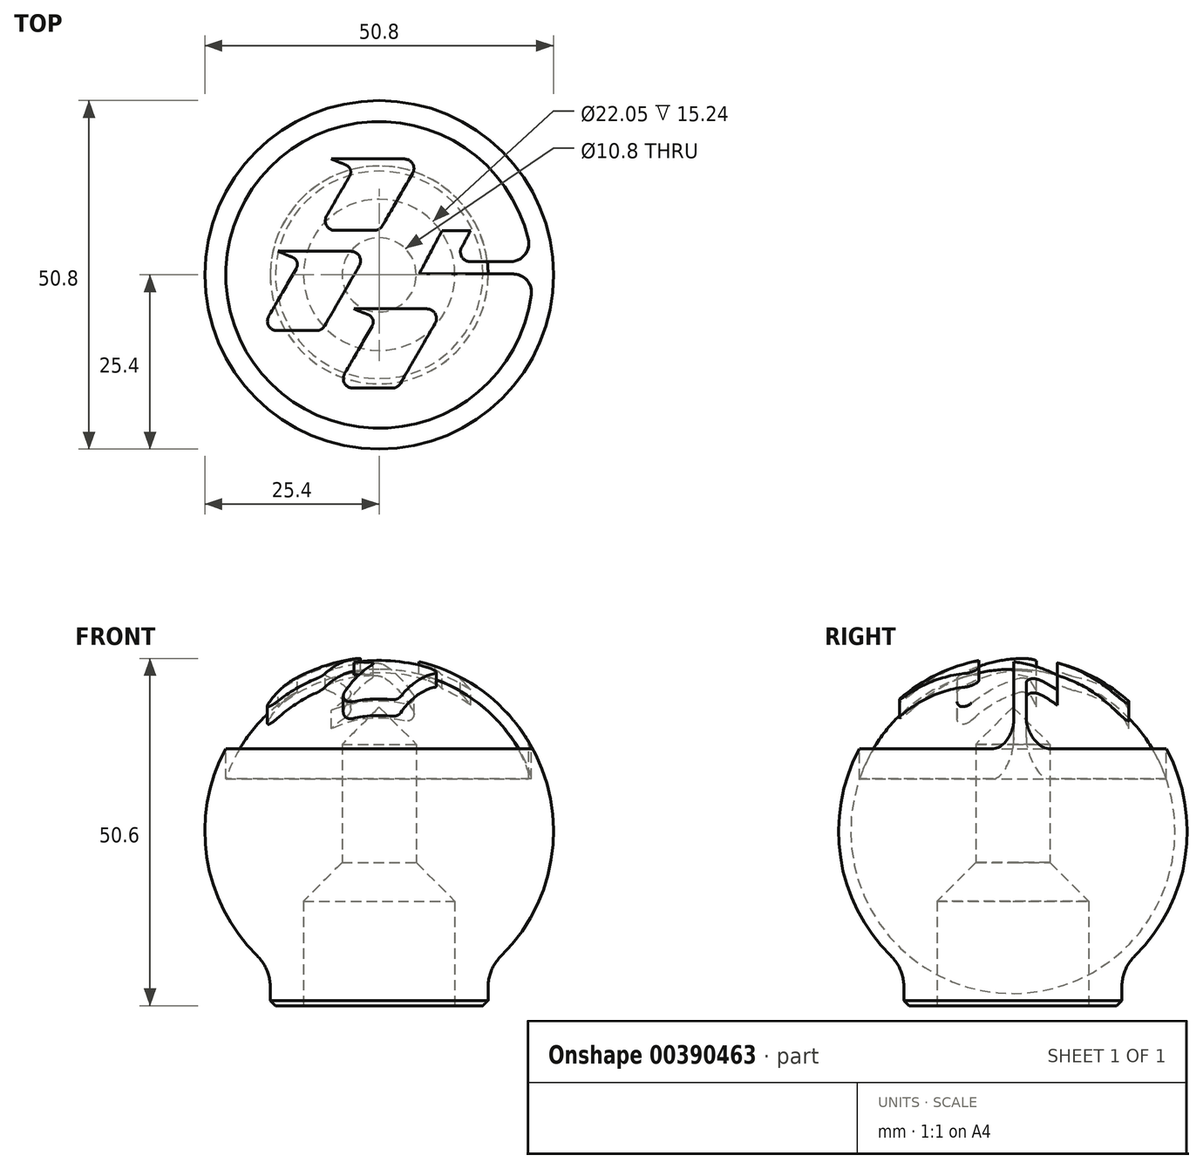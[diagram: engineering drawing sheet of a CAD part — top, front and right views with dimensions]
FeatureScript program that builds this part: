
annotation { "Feature Type Name" : "Feature", "Feature Type Description" : "" }
export const myFeature = defineFeature(function(context is Context, id is Id, definition is map)
    precondition{}
    {
        {
            var Q0;
            Q0=qCreatedBy(makeId("Top.planeOp"),FACE);
            cPlane(context, id + "F0", {"entities" : qUnion([Q0]), "cplaneType" : CPlaneType.OFFSET, "offset" : 50.8 * mm, "width" : 152.4 * mm, "height" : 152.4 * mm});
        }
        {
            var Q0;
            Q0=qCreatedBy(makeId("Front.planeOp"),FACE);
            var sketch = newSketch(context, id + "F1", { "sketchPlane" : qUnion([Q0])});
            skLineSegment(sketch, "E0", {"start": v(0, 0) * mm, "end": v(0, 50.8) * mm});
            skArc(sketch, "E1", {"start": v(17.78, 7.26) * mm, "mid": v(23.51, 35) * mm, "end": v(0, 50.8) * mm});
            skArc(sketch, "E2", {"start": v(17.78, 7.26) * mm, "mid": v(16.37, 5.19) * mm, "end": v(15.88, 2.73) * mm});
            skLineSegment(sketch, "E3", {"start": v(15.88, 2.73) * mm, "end": v(15.88, 0) * mm});
            skLineSegment(sketch, "E4", {"start": v(15.88, 0) * mm, "end": v(0, 0) * mm});
            skSolve(sketch);
        }
        {
            var Q0;
            Q0=makeQuery(id+"F1.imprint","IMPRINT",FACE,{"disambiguationData":[TD([[makeQuery(id+"F1.imprint","IMPRINT",EDGE,{"derivedFrom":sQuery(id+"F1.wireOp",EDGE,"E0")}),-1.0]])]});
            var Q1;
            Q1=sQuery(id+"F1.wireOp",EDGE,"E0");
            revolve(context, id + "F2", {"entities" : qUnion([Q0]), "axis" : qUnion([Q1]), "revolveType" : RevolveType.FULL});
        }
        {
            var Q0;
            Q0=makeQuery(id+"F2.opRevolve","SWEPT_FACE",FACE,{"disambiguationData":[OSD([sQuery(id+"F1.wireOp",EDGE,"E4")])]});
            var sketch = newSketch(context, id + "F3", { "sketchPlane" : qUnion([Q0])});
            skCircle(sketch, "E5", {"center": v(0, 0) * mm, "radius": 5.4 * mm});
            skSolve(sketch);
        }
        {
            var Q0;
            Q0=makeQuery(id+"F2.opRevolve","SWEPT_FACE",FACE,{"disambiguationData":[OSD([sQuery(id+"F1.wireOp",EDGE,"E4")])]});
            var sketch = newSketch(context, id + "F4", { "sketchPlane" : qUnion([Q0])});
            skCircle(sketch, "E6", {"center": v(0, 0) * mm, "radius": 11.02 * mm});
            skSolve(sketch);
        }
        {
            var Q0;
            Q0=qCreatedBy(makeId("Top.planeOp"),FACE);
            var sketch = newSketch(context, id + "F5", { "sketchPlane" : qUnion([Q0])});
            skArc(sketch, "E7", {"start": v(21.6, 5.2) * mm, "mid": v(-22.2, -1.18) * mm, "end": v(22.04, -2.87) * mm});
            skArc(sketch, "E8", {"start": v(18.88, 5.56) * mm, "mid": v(-19.65, -1.14) * mm, "end": v(19.4, -3.35) * mm});
            skLineSegment(sketch, "E9", {"start": v(-6.33, 16.76) * mm, "end": v(3.67, 16.76) * mm});
            skLineSegment(sketch, "E10", {"start": v(4.77, 14.86) * mm, "end": v(0.37, 7.24) * mm});
            skLineSegment(sketch, "E11", {"start": v(-0.73, 6.6) * mm, "end": v(-6.45, 6.6) * mm});
            skLineSegment(sketch, "E12", {"start": v(-7.55, 8.5) * mm, "end": v(-4.19, 14.34) * mm});
            skLineSegment(sketch, "E13", {"start": v(-4.81, 16.15) * mm, "end": v(-6.33, 16.76) * mm});
            skLineSegment(sketch, "E14", {"start": v(-14.1, 3.3) * mm, "end": v(-4.1, 3.3) * mm});
            skLineSegment(sketch, "E15", {"start": v(-3, 1.4) * mm, "end": v(-8.07, -7.37) * mm});
            skLineSegment(sketch, "E16", {"start": v(-9.17, -8) * mm, "end": v(-14.88, -8) * mm});
            skLineSegment(sketch, "E17", {"start": v(-15.98, -6.1) * mm, "end": v(-11.96, 0.88) * mm});
            skLineSegment(sketch, "E18", {"start": v(-12.58, 2.69) * mm, "end": v(-14.1, 3.3) * mm});
            skLineSegment(sketch, "E19", {"start": v(-3.05, -5.08) * mm, "end": v(6.94, -5.08) * mm});
            skLineSegment(sketch, "E20", {"start": v(8.04, -6.98) * mm, "end": v(2.98, -15.75) * mm});
            skLineSegment(sketch, "E21", {"start": v(1.88, -16.38) * mm, "end": v(-3.83, -16.38) * mm});
            skLineSegment(sketch, "E22", {"start": v(-4.93, -14.48) * mm, "end": v(-0.9, -7.5) * mm});
            skLineSegment(sketch, "E23", {"start": v(-1.53, -5.7) * mm, "end": v(-3.05, -5.08) * mm});
            skPoint(sketch, "E24.visualSharp", {"position": v(5.87, 16.76) * mm});
            skArc(sketch, "E24.filletArc", {"start": v(4.77, 14.86) * mm, "mid": v(4.77, 16.13) * mm, "end": v(3.67, 16.76) * mm});
            skPoint(sketch, "E25.visualSharp", {"position": v(-3.46, 15.6) * mm});
            skArc(sketch, "E25.filletArc", {"start": v(-4.19, 14.34) * mm, "mid": v(-4.09, 15.39) * mm, "end": v(-4.81, 16.15) * mm});
            skPoint(sketch, "E26.visualSharp", {"position": v(-8.65, 6.6) * mm});
            skArc(sketch, "E26.filletArc", {"start": v(-7.55, 8.5) * mm, "mid": v(-7.55, 7.24) * mm, "end": v(-6.45, 6.6) * mm});
            skPoint(sketch, "E27.visualSharp", {"position": v(0, 6.6) * mm});
            skArc(sketch, "E27.filletArc", {"start": v(-0.73, 6.6) * mm, "mid": v(-0.1, 6.77) * mm, "end": v(0.37, 7.24) * mm});
            skPoint(sketch, "E28.visualSharp", {"position": v(-17.08, -8) * mm});
            skArc(sketch, "E28.filletArc", {"start": v(-15.98, -6.1) * mm, "mid": v(-15.98, -7.37) * mm, "end": v(-14.88, -8) * mm});
            skPoint(sketch, "E29.visualSharp", {"position": v(-11.23, 2.14) * mm});
            skArc(sketch, "E29.filletArc", {"start": v(-11.96, 0.88) * mm, "mid": v(-11.86, 1.93) * mm, "end": v(-12.58, 2.69) * mm});
            skPoint(sketch, "E30.visualSharp", {"position": v(-1.9, 3.3) * mm});
            skArc(sketch, "E30.filletArc", {"start": v(-3, 1.4) * mm, "mid": v(-3, 2.67) * mm, "end": v(-4.1, 3.3) * mm});
            skPoint(sketch, "E31.visualSharp", {"position": v(-8.43, -8) * mm});
            skArc(sketch, "E31.filletArc", {"start": v(-9.17, -8) * mm, "mid": v(-8.53, -7.83) * mm, "end": v(-8.07, -7.37) * mm});
            skPoint(sketch, "E32.visualSharp", {"position": v(-6.03, -16.38) * mm});
            skArc(sketch, "E32.filletArc", {"start": v(-4.93, -14.48) * mm, "mid": v(-4.93, -15.75) * mm, "end": v(-3.83, -16.38) * mm});
            skPoint(sketch, "E33.visualSharp", {"position": v(-0.18, -6.24) * mm});
            skArc(sketch, "E33.filletArc", {"start": v(-0.9, -7.5) * mm, "mid": v(-0.8, -6.46) * mm, "end": v(-1.53, -5.7) * mm});
            skPoint(sketch, "E34.visualSharp", {"position": v(9.14, -5.08) * mm});
            skArc(sketch, "E34.filletArc", {"start": v(8.04, -6.98) * mm, "mid": v(8.04, -5.71) * mm, "end": v(6.94, -5.08) * mm});
            skPoint(sketch, "E35.visualSharp", {"position": v(2.62, -16.38) * mm});
            skArc(sketch, "E35.filletArc", {"start": v(1.88, -16.38) * mm, "mid": v(2.52, -16.21) * mm, "end": v(2.98, -15.75) * mm});
            skLineSegment(sketch, "E36", {"start": v(17.66, 3.93) * mm, "end": v(14.24, 3.93) * mm});
            skLineSegment(sketch, "E37", {"start": v(14.24, 3.93) * mm, "end": v(15.65, 6.43) * mm});
            skLineSegment(sketch, "E38", {"start": v(14.55, 8.33) * mm, "end": v(4.49, 8.33) * mm});
            skLineSegment(sketch, "E39", {"start": v(4.49, 8.33) * mm, "end": v(6.07, 7.6) * mm});
            skLineSegment(sketch, "E40", {"start": v(6.67, 5.86) * mm, "end": v(3.65, 0) * mm});
            skLineSegment(sketch, "E41", {"start": v(4.78, -1.86) * mm, "end": v(18.15, -1.86) * mm});
            skPoint(sketch, "E42.visualSharp", {"position": v(7.28, 7.04) * mm});
            skArc(sketch, "E42.filletArc", {"start": v(6.67, 5.86) * mm, "mid": v(6.74, 6.86) * mm, "end": v(6.07, 7.6) * mm});
            skPoint(sketch, "E43.visualSharp", {"position": v(2.7, -1.86) * mm});
            skArc(sketch, "E43.filletArc", {"start": v(3.65, 0) * mm, "mid": v(3.7, -1.25) * mm, "end": v(4.78, -1.86) * mm});
            skPoint(sketch, "E44.visualSharp", {"position": v(16.72, 8.33) * mm});
            skArc(sketch, "E44.filletArc", {"start": v(15.65, 6.43) * mm, "mid": v(15.64, 7.7) * mm, "end": v(14.55, 8.33) * mm});
            skLineSegment(sketch, "E45", {"start": v(19.14, 2.06) * mm, "end": v(13.24, 2.06) * mm});
            skLineSegment(sketch, "E46", {"start": v(12.12, 3.94) * mm, "end": v(13.56, 6.6) * mm});
            skLineSegment(sketch, "E47", {"start": v(13.56, 6.6) * mm, "end": v(9.1, 6.6) * mm});
            skLineSegment(sketch, "E48", {"start": v(9.1, 6.6) * mm, "end": v(5.6, 0) * mm});
            skLineSegment(sketch, "E49", {"start": v(5.6, 0) * mm, "end": v(19.52, 0) * mm});
            skPoint(sketch, "E50.visualSharp", {"position": v(19.29, 3.93) * mm});
            skArc(sketch, "E50.filletArc", {"start": v(17.66, 3.93) * mm, "mid": v(18.68, 4.44) * mm, "end": v(18.88, 5.56) * mm});
            skPoint(sketch, "E51.visualSharp", {"position": v(19.6, -1.86) * mm});
            skArc(sketch, "E51.filletArc", {"start": v(19.4, -3.35) * mm, "mid": v(19.12, -2.31) * mm, "end": v(18.15, -1.86) * mm});
            skPoint(sketch, "E52.visualSharp", {"position": v(22.13, 2.06) * mm});
            skArc(sketch, "E52.filletArc", {"start": v(19.14, 2.06) * mm, "mid": v(21.13, 3.03) * mm, "end": v(21.6, 5.2) * mm});
            skPoint(sketch, "E53.visualSharp", {"position": v(22.23, 0) * mm});
            skArc(sketch, "E53.filletArc", {"start": v(22.04, -2.87) * mm, "mid": v(21.43, -0.86) * mm, "end": v(19.52, 0) * mm});
            skLineSegment(sketch, "E54", {"start": v(-1.08, 8.22) * mm, "end": v(2.81, 15.15) * mm});
            skLineSegment(sketch, "E55", {"start": v(2.81, 15.15) * mm, "end": v(-1.67, 15.15) * mm});
            skLineSegment(sketch, "E56", {"start": v(-1.67, 15.15) * mm, "end": v(-5.68, 8.2) * mm});
            skLineSegment(sketch, "E57", {"start": v(-5.68, 8.2) * mm, "end": v(-1.08, 8.22) * mm});
            skLineSegment(sketch, "E58", {"start": v(-4.84, 1.6) * mm, "end": v(-9.4, 1.6) * mm});
            skLineSegment(sketch, "E59", {"start": v(-9.4, 1.6) * mm, "end": v(-13.91, -6.2) * mm});
            skLineSegment(sketch, "E60", {"start": v(-13.91, -6.2) * mm, "end": v(-9.35, -6.2) * mm});
            skLineSegment(sketch, "E61", {"start": v(-9.35, -6.2) * mm, "end": v(-4.84, 1.6) * mm});
            skLineSegment(sketch, "E62", {"start": v(1.76, -6.8) * mm, "end": v(-2.86, -14.8) * mm});
            skLineSegment(sketch, "E63", {"start": v(-2.86, -14.8) * mm, "end": v(1.4, -14.8) * mm});
            skLineSegment(sketch, "E64", {"start": v(1.4, -14.8) * mm, "end": v(6.21, -6.78) * mm});
            skLineSegment(sketch, "E65", {"start": v(6.21, -6.78) * mm, "end": v(1.76, -6.8) * mm});
            skPoint(sketch, "E66.visualSharp", {"position": v(11.1, 2.06) * mm});
            skArc(sketch, "E66.filletArc", {"start": v(12.12, 3.94) * mm, "mid": v(12.14, 2.68) * mm, "end": v(13.24, 2.06) * mm});
            skSolve(sketch);
        }
        {
            var Q0;
            Q0=qCreatedBy(makeId("Right.planeOp"),FACE);
            var sketch = newSketch(context, id + "F6", { "sketchPlane" : qUnion([Q0])});
            skArc(sketch, "E67", {"start": v(26.16, 25.4) * mm, "mid": v(18.5, 43.9) * mm, "end": v(0, 51.56) * mm});
            skLineSegment(sketch, "E68", {"start": v(0, 25.4) * mm, "end": v(26.16, 25.4) * mm, "construction": true});
            skLineSegment(sketch, "E69", {"start": v(0, 25.4) * mm, "end": v(0, 51.56) * mm, "construction": true});
            skSolve(sketch);
        }
        {
            var Q0;
            Q0=sQuery(id+"F6.wireOp",EDGE,"E67");
            var Q1;
            Q1=sQuery(id+"F6.wireOp",EDGE,"E69");
            revolve(context, id + "F7", {"bodyType" : ToolBodyType.SURFACE, "surfaceEntities" : qUnion([Q0]), "axis" : qUnion([Q1]), "revolveType" : RevolveType.FULL});
        }
        {
            var Q0;
            Q0=makeQuery(id+"F2.opRevolve","SWEPT_EDGE",EDGE,{"disambiguationData":[OSD([sQuery(id+"F1.wireOp",EDGE,"E3"),sQuery(id+"F1.wireOp",EDGE,"E4")])]});
            chamfer(context, id + "F8", {"entities" : qUnion([Q0]), "width" : 0.76 * mm, "tangentPropagation" : true});
        }
        {
            var Q0;
            Q0=makeQuery(id+"F7.opRevolve","SWEPT_BODY",BODY,{"disambiguationData":[OSD([sQuery(id+"F6.wireOp",EDGE,"E67")])]});
            deleteBodies(context, id + "F9", {"entities" : qUnion([Q0])});
        }
        {
            var Q0;
            Q0=makeQuery(id+"F4.imprint","IMPRINT",FACE,{"disambiguationData":[TD([[makeQuery(id+"F4.imprint","IMPRINT",EDGE,{"derivedFrom":sQuery(id+"F4.wireOp",EDGE,"E6")}),1.0]])]});
            extrude(context, id + "F10", {"entities" : qUnion([Q0]), "operationType" : NewBodyOperationType.REMOVE, "oppositeDirection" : true, "depth" : 15.24 * mm});
        }
        {
            var Q0;
            Q0=makeQuery(id+"F3.imprint","IMPRINT",FACE,{"disambiguationData":[TD([[makeQuery(id+"F3.imprint","IMPRINT",EDGE,{"derivedFrom":sQuery(id+"F3.wireOp",EDGE,"E5")}),1.0]])]});
            extrude(context, id + "F11", {"entities" : qUnion([Q0]), "operationType" : NewBodyOperationType.REMOVE, "oppositeDirection" : true, "depth" : 38.1 * mm});
        }
        {
            var Q0;
            Q0=qCreatedBy(makeId("Front.planeOp"),FACE);
            var sketch = newSketch(context, id + "F12", { "sketchPlane" : qUnion([Q0])});
            skLineSegment(sketch, "E70", {"start": v(0, 43.5) * mm, "end": v(-5.4, 38.1) * mm});
            skLineSegment(sketch, "E71.0", {"start": v(11.02, 15.24) * mm, "end": v(-11.02, 15.24) * mm, "construction": true});
            skLineSegment(sketch, "E72", {"start": v(-11.02, 15.24) * mm, "end": v(-5.4, 20.86) * mm});
            skLineSegment(sketch, "E73", {"start": v(0, 43.5) * mm, "end": v(0, 15.24) * mm});
            skLineSegment(sketch, "E74", {"start": v(0, 15.24) * mm, "end": v(-11.02, 15.24) * mm});
            skLineSegment(sketch, "E75", {"start": v(-5.4, 38.1) * mm, "end": v(-5.4, 20.86) * mm});
            skSolve(sketch);
        }
        {
            var Q0;
            Q0=makeQuery(id+"F12.imprint","IMPRINT",FACE,{"disambiguationData":[TD([[makeQuery(id+"F12.imprint","IMPRINT",EDGE,{"derivedFrom":sQuery(id+"F12.wireOp",EDGE,"E70")}),1.0]])]});
            var Q1;
            Q1=sQuery(id+"F12.wireOp",EDGE,"E73");
            revolve(context, id + "F13", {"operationType" : NewBodyOperationType.REMOVE, "entities" : qUnion([Q0]), "axis" : qUnion([Q1]), "revolveType" : RevolveType.FULL, "oppositeDirection" : true});
        }
        {
            var Q0;
            Q0=qCreatedBy(id+"F0.planeOp",FACE);
            var sketch = newSketch(context, id + "F14", { "sketchPlane" : qUnion([Q0])});
            skArc(sketch, "E76.0", {"start": v(19.4, -3.35) * mm, "mid": v(-19.65, -1.14) * mm, "end": v(18.88, 5.56) * mm, "construction": true});
            skArc(sketch, "E77.0", {"start": v(22.04, -2.87) * mm, "mid": v(-22.2, -1.18) * mm, "end": v(21.6, 5.2) * mm, "construction": true});
            skArc(sketch, "E78.0", {"start": v(21.6, 5.2) * mm, "mid": v(21.13, 3.03) * mm, "end": v(19.14, 2.06) * mm, "construction": true});
            skLineSegment(sketch, "E78.1", {"start": v(13.24, 2.06) * mm, "end": v(19.14, 2.06) * mm, "construction": true});
            skLineSegment(sketch, "E78.2", {"start": v(14.24, 3.93) * mm, "end": v(17.66, 3.93) * mm, "construction": true});
            skArc(sketch, "E78.3", {"start": v(18.88, 5.56) * mm, "mid": v(18.68, 4.44) * mm, "end": v(17.66, 3.93) * mm, "construction": true});
            skLineSegment(sketch, "E78.4", {"start": v(15.65, 6.43) * mm, "end": v(14.24, 3.93) * mm, "construction": true});
            skArc(sketch, "E78.5", {"start": v(14.55, 8.33) * mm, "mid": v(15.64, 7.7) * mm, "end": v(15.65, 6.43) * mm, "construction": true});
            skLineSegment(sketch, "E78.6", {"start": v(4.49, 8.33) * mm, "end": v(14.55, 8.33) * mm, "construction": true});
            skLineSegment(sketch, "E78.7", {"start": v(9.1, 6.6) * mm, "end": v(13.56, 6.6) * mm, "construction": true});
            skLineSegment(sketch, "E78.8", {"start": v(5.6, 0) * mm, "end": v(9.1, 6.6) * mm, "construction": true});
            skLineSegment(sketch, "E78.9", {"start": v(13.56, 6.6) * mm, "end": v(12.12, 3.94) * mm, "construction": true});
            skArc(sketch, "E78.10", {"start": v(13.24, 2.06) * mm, "mid": v(12.14, 2.68) * mm, "end": v(12.12, 3.94) * mm, "construction": true});
            skLineSegment(sketch, "E78.11", {"start": v(19.52, 0) * mm, "end": v(5.6, 0) * mm, "construction": true});
            skArc(sketch, "E78.12", {"start": v(19.52, 0) * mm, "mid": v(21.43, -0.86) * mm, "end": v(22.04, -2.87) * mm, "construction": true});
            skArc(sketch, "E78.15", {"start": v(18.15, -1.86) * mm, "mid": v(19.12, -2.31) * mm, "end": v(19.4, -3.35) * mm, "construction": true});
            skLineSegment(sketch, "E78.16", {"start": v(18.15, -1.86) * mm, "end": v(4.78, -1.86) * mm, "construction": true});
            skArc(sketch, "E78.17", {"start": v(4.78, -1.86) * mm, "mid": v(3.7, -1.25) * mm, "end": v(3.65, 0) * mm, "construction": true});
            skLineSegment(sketch, "E78.18", {"start": v(3.65, 0) * mm, "end": v(6.67, 5.86) * mm, "construction": true});
            skArc(sketch, "E78.19", {"start": v(6.07, 7.6) * mm, "mid": v(6.74, 6.86) * mm, "end": v(6.67, 5.86) * mm, "construction": true});
            skLineSegment(sketch, "E78.20", {"start": v(6.07, 7.6) * mm, "end": v(4.49, 8.33) * mm, "construction": true});
            skLineSegment(sketch, "E79.0", {"start": v(0.37, 7.24) * mm, "end": v(4.77, 14.86) * mm, "construction": true});
            skArc(sketch, "E79.1", {"start": v(3.67, 16.76) * mm, "mid": v(4.77, 16.13) * mm, "end": v(4.77, 14.86) * mm, "construction": true});
            skLineSegment(sketch, "E79.2", {"start": v(3.67, 16.76) * mm, "end": v(-6.33, 16.76) * mm, "construction": true});
            skArc(sketch, "E79.3", {"start": v(-4.81, 16.15) * mm, "mid": v(-4.09, 15.39) * mm, "end": v(-4.19, 14.34) * mm, "construction": true});
            skLineSegment(sketch, "E79.4", {"start": v(-6.33, 16.76) * mm, "end": v(-4.81, 16.15) * mm, "construction": true});
            skLineSegment(sketch, "E79.5", {"start": v(-4.19, 14.34) * mm, "end": v(-7.55, 8.5) * mm, "construction": true});
            skArc(sketch, "E79.6", {"start": v(-6.45, 6.6) * mm, "mid": v(-7.55, 7.24) * mm, "end": v(-7.55, 8.5) * mm, "construction": true});
            skLineSegment(sketch, "E79.7", {"start": v(-6.45, 6.6) * mm, "end": v(-0.73, 6.6) * mm, "construction": true});
            skArc(sketch, "E79.8", {"start": v(0.37, 7.24) * mm, "mid": v(-0.1, 6.77) * mm, "end": v(-0.73, 6.6) * mm, "construction": true});
            skLineSegment(sketch, "E79.9", {"start": v(2.81, 15.15) * mm, "end": v(-1.08, 8.22) * mm, "construction": true});
            skLineSegment(sketch, "E79.10", {"start": v(-1.08, 8.22) * mm, "end": v(-5.68, 8.2) * mm, "construction": true});
            skLineSegment(sketch, "E79.11", {"start": v(-5.68, 8.2) * mm, "end": v(-1.67, 15.15) * mm, "construction": true});
            skLineSegment(sketch, "E79.12", {"start": v(-1.67, 15.15) * mm, "end": v(2.81, 15.15) * mm, "construction": true});
            skLineSegment(sketch, "E79.13", {"start": v(-4.1, 3.3) * mm, "end": v(-14.1, 3.3) * mm, "construction": true});
            skArc(sketch, "E79.14", {"start": v(-4.1, 3.3) * mm, "mid": v(-3, 2.67) * mm, "end": v(-3, 1.4) * mm, "construction": true});
            skLineSegment(sketch, "E79.15", {"start": v(-8.07, -7.37) * mm, "end": v(-3, 1.4) * mm, "construction": true});
            skLineSegment(sketch, "E79.16", {"start": v(-4.84, 1.6) * mm, "end": v(-9.35, -6.2) * mm, "construction": true});
            skLineSegment(sketch, "E79.17", {"start": v(-9.4, 1.6) * mm, "end": v(-4.84, 1.6) * mm, "construction": true});
            skLineSegment(sketch, "E79.18", {"start": v(-13.91, -6.2) * mm, "end": v(-9.4, 1.6) * mm, "construction": true});
            skLineSegment(sketch, "E79.19", {"start": v(-9.35, -6.2) * mm, "end": v(-13.91, -6.2) * mm, "construction": true});
            skArc(sketch, "E79.20", {"start": v(-8.07, -7.37) * mm, "mid": v(-8.53, -7.83) * mm, "end": v(-9.17, -8) * mm, "construction": true});
            skLineSegment(sketch, "E79.21", {"start": v(-14.88, -8) * mm, "end": v(-9.17, -8) * mm, "construction": true});
            skArc(sketch, "E79.22", {"start": v(-14.88, -8) * mm, "mid": v(-15.98, -7.37) * mm, "end": v(-15.98, -6.1) * mm, "construction": true});
            skLineSegment(sketch, "E79.23", {"start": v(-11.96, 0.88) * mm, "end": v(-15.98, -6.1) * mm, "construction": true});
            skArc(sketch, "E79.24", {"start": v(-12.58, 2.69) * mm, "mid": v(-11.86, 1.93) * mm, "end": v(-11.96, 0.88) * mm, "construction": true});
            skLineSegment(sketch, "E79.25", {"start": v(-14.1, 3.3) * mm, "end": v(-12.58, 2.69) * mm, "construction": true});
            skLineSegment(sketch, "E80.0", {"start": v(6.94, -5.08) * mm, "end": v(-3.05, -5.08) * mm, "construction": true});
            skArc(sketch, "E80.1", {"start": v(6.94, -5.08) * mm, "mid": v(8.04, -5.71) * mm, "end": v(8.04, -6.98) * mm, "construction": true});
            skLineSegment(sketch, "E80.2", {"start": v(2.98, -15.75) * mm, "end": v(8.04, -6.98) * mm, "construction": true});
            skLineSegment(sketch, "E80.3", {"start": v(6.21, -6.78) * mm, "end": v(1.4, -14.8) * mm, "construction": true});
            skLineSegment(sketch, "E80.4", {"start": v(1.76, -6.8) * mm, "end": v(6.21, -6.78) * mm, "construction": true});
            skLineSegment(sketch, "E80.5", {"start": v(-2.86, -14.8) * mm, "end": v(1.76, -6.8) * mm, "construction": true});
            skArc(sketch, "E80.6", {"start": v(-1.53, -5.7) * mm, "mid": v(-0.8, -6.46) * mm, "end": v(-0.9, -7.5) * mm, "construction": true});
            skLineSegment(sketch, "E80.7", {"start": v(-3.05, -5.08) * mm, "end": v(-1.53, -5.7) * mm, "construction": true});
            skLineSegment(sketch, "E80.8", {"start": v(-0.9, -7.5) * mm, "end": v(-4.93, -14.48) * mm, "construction": true});
            skArc(sketch, "E80.9", {"start": v(-3.83, -16.38) * mm, "mid": v(-4.93, -15.75) * mm, "end": v(-4.93, -14.48) * mm, "construction": true});
            skLineSegment(sketch, "E80.10", {"start": v(-3.83, -16.38) * mm, "end": v(1.88, -16.38) * mm, "construction": true});
            skLineSegment(sketch, "E80.11", {"start": v(1.4, -14.8) * mm, "end": v(-2.86, -14.8) * mm, "construction": true});
            skArc(sketch, "E80.12", {"start": v(2.98, -15.75) * mm, "mid": v(2.52, -16.21) * mm, "end": v(1.88, -16.38) * mm, "construction": true});
            skArc(sketch, "E81.0", {"start": v(19.52, 0.13) * mm, "mid": v(21.52, -0.78) * mm, "end": v(22.17, -2.88) * mm});
            skLineSegment(sketch, "E81.1", {"start": v(19.52, 0.13) * mm, "end": v(5.82, 0.13) * mm});
            skArc(sketch, "E81.2", {"start": v(22.17, -2.88) * mm, "mid": v(-22.32, -1.2) * mm, "end": v(21.73, 5.23) * mm});
            skLineSegment(sketch, "E81.3", {"start": v(5.82, 0.13) * mm, "end": v(9.17, 6.47) * mm});
            skLineSegment(sketch, "E81.4", {"start": v(9.17, 6.47) * mm, "end": v(13.35, 6.47) * mm});
            skArc(sketch, "E81.5", {"start": v(21.73, 5.23) * mm, "mid": v(21.23, 2.95) * mm, "end": v(19.14, 1.94) * mm});
            skLineSegment(sketch, "E81.6", {"start": v(13.24, 1.94) * mm, "end": v(19.14, 1.94) * mm});
            skArc(sketch, "E81.7", {"start": v(13.24, 1.94) * mm, "mid": v(12.04, 2.62) * mm, "end": v(12, 4) * mm});
            skLineSegment(sketch, "E81.8", {"start": v(13.35, 6.47) * mm, "end": v(12, 4) * mm});
            skLineSegment(sketch, "E82.0", {"start": v(15.76, 6.37) * mm, "end": v(14.46, 4.06) * mm});
            skLineSegment(sketch, "E82.1", {"start": v(18.15, -1.99) * mm, "end": v(4.78, -1.99) * mm});
            skArc(sketch, "E82.2", {"start": v(18.15, -1.99) * mm, "mid": v(19.02, -2.4) * mm, "end": v(19.27, -3.32) * mm});
            skArc(sketch, "E82.3", {"start": v(19.27, -3.32) * mm, "mid": v(-19.53, -1.13) * mm, "end": v(18.76, 5.53) * mm});
            skArc(sketch, "E82.4", {"start": v(18.76, 5.53) * mm, "mid": v(18.58, 4.52) * mm, "end": v(17.66, 4.06) * mm});
            skArc(sketch, "E82.5", {"start": v(4.78, -1.99) * mm, "mid": v(3.59, -1.32) * mm, "end": v(3.54, 0.05) * mm});
            skLineSegment(sketch, "E82.6", {"start": v(14.46, 4.06) * mm, "end": v(17.66, 4.06) * mm});
            skLineSegment(sketch, "E82.7", {"start": v(3.54, 0.05) * mm, "end": v(6.56, 5.92) * mm});
            skArc(sketch, "E82.8", {"start": v(6.02, 7.48) * mm, "mid": v(6.62, 6.82) * mm, "end": v(6.56, 5.92) * mm});
            skLineSegment(sketch, "E82.9", {"start": v(6.02, 7.48) * mm, "end": v(3.9, 8.45) * mm});
            skLineSegment(sketch, "E82.10", {"start": v(3.9, 8.45) * mm, "end": v(14.55, 8.45) * mm});
            skArc(sketch, "E82.11", {"start": v(14.55, 8.45) * mm, "mid": v(15.75, 7.76) * mm, "end": v(15.76, 6.37) * mm});
            skArc(sketch, "E83.0", {"start": v(-7.96, -7.43) * mm, "mid": v(-8.47, -7.94) * mm, "end": v(-9.17, -8.13) * mm});
            skLineSegment(sketch, "E83.1", {"start": v(-14.88, -8.13) * mm, "end": v(-9.17, -8.13) * mm});
            skLineSegment(sketch, "E83.2", {"start": v(-7.96, -7.43) * mm, "end": v(-2.9, 1.33) * mm});
            skArc(sketch, "E83.3", {"start": v(-14.88, -8.13) * mm, "mid": v(-16.1, -7.43) * mm, "end": v(-16.1, -6.03) * mm});
            skLineSegment(sketch, "E83.4", {"start": v(-12.07, 0.94) * mm, "end": v(-16.1, -6.03) * mm});
            skArc(sketch, "E83.5", {"start": v(-4.1, 3.43) * mm, "mid": v(-2.9, 2.73) * mm, "end": v(-2.9, 1.33) * mm});
            skLineSegment(sketch, "E83.6", {"start": v(-4.1, 3.43) * mm, "end": v(-14.75, 3.43) * mm});
            skLineSegment(sketch, "E83.7", {"start": v(-14.75, 3.43) * mm, "end": v(-12.63, 2.57) * mm});
            skArc(sketch, "E83.8", {"start": v(-12.63, 2.57) * mm, "mid": v(-11.98, 1.88) * mm, "end": v(-12.07, 0.94) * mm});
            skArc(sketch, "E84.0", {"start": v(0.48, 7.18) * mm, "mid": v(-0.03, 6.66) * mm, "end": v(-0.73, 6.48) * mm});
            skLineSegment(sketch, "E84.1", {"start": v(-6.45, 6.48) * mm, "end": v(-0.73, 6.48) * mm});
            skLineSegment(sketch, "E84.2", {"start": v(0.48, 7.18) * mm, "end": v(4.88, 14.8) * mm});
            skArc(sketch, "E84.3", {"start": v(-6.45, 6.48) * mm, "mid": v(-7.66, 7.18) * mm, "end": v(-7.66, 8.57) * mm});
            skLineSegment(sketch, "E84.4", {"start": v(-4.3, 14.4) * mm, "end": v(-7.66, 8.57) * mm});
            skArc(sketch, "E84.5", {"start": v(3.67, 16.9) * mm, "mid": v(4.88, 16.2) * mm, "end": v(4.88, 14.8) * mm});
            skLineSegment(sketch, "E84.6", {"start": v(3.67, 16.9) * mm, "end": v(-6.98, 16.9) * mm});
            skLineSegment(sketch, "E84.7", {"start": v(-6.98, 16.9) * mm, "end": v(-4.86, 16.03) * mm});
            skArc(sketch, "E84.8", {"start": v(-4.86, 16.03) * mm, "mid": v(-4.2, 15.35) * mm, "end": v(-4.3, 14.4) * mm});
            skArc(sketch, "E85.0", {"start": v(-1.58, -5.81) * mm, "mid": v(-0.93, -6.5) * mm, "end": v(-1.02, -7.44) * mm});
            skLineSegment(sketch, "E85.1", {"start": v(-3.7, -4.95) * mm, "end": v(-1.58, -5.81) * mm});
            skLineSegment(sketch, "E85.2", {"start": v(-1.02, -7.44) * mm, "end": v(-5.04, -14.41) * mm});
            skLineSegment(sketch, "E85.3", {"start": v(6.94, -4.95) * mm, "end": v(-3.7, -4.95) * mm});
            skArc(sketch, "E85.4", {"start": v(6.94, -4.95) * mm, "mid": v(8.15, -5.65) * mm, "end": v(8.15, -7.05) * mm});
            skArc(sketch, "E85.5", {"start": v(-3.83, -16.51) * mm, "mid": v(-5.04, -15.81) * mm, "end": v(-5.04, -14.41) * mm});
            skLineSegment(sketch, "E85.6", {"start": v(-3.83, -16.51) * mm, "end": v(1.88, -16.51) * mm});
            skArc(sketch, "E85.7", {"start": v(3.1, -15.81) * mm, "mid": v(2.58, -16.32) * mm, "end": v(1.88, -16.51) * mm});
            skLineSegment(sketch, "E85.8", {"start": v(3.1, -15.81) * mm, "end": v(8.15, -7.05) * mm});
            skLineSegment(sketch, "E86.0", {"start": v(1.84, -6.93) * mm, "end": v(5.99, -6.9) * mm});
            skLineSegment(sketch, "E86.1", {"start": v(-2.64, -14.68) * mm, "end": v(1.84, -6.93) * mm});
            skLineSegment(sketch, "E86.2", {"start": v(1.33, -14.68) * mm, "end": v(-2.64, -14.68) * mm});
            skLineSegment(sketch, "E86.3", {"start": v(5.99, -6.9) * mm, "end": v(1.33, -14.68) * mm});
            skLineSegment(sketch, "E87.0", {"start": v(-5.06, 1.47) * mm, "end": v(-9.42, -6.08) * mm});
            skLineSegment(sketch, "E87.1", {"start": v(-9.33, 1.47) * mm, "end": v(-5.06, 1.47) * mm});
            skLineSegment(sketch, "E87.2", {"start": v(-13.7, -6.08) * mm, "end": v(-9.33, 1.47) * mm});
            skLineSegment(sketch, "E87.3", {"start": v(-9.42, -6.08) * mm, "end": v(-13.7, -6.08) * mm});
            skLineSegment(sketch, "E88.0", {"start": v(2.6, 15.03) * mm, "end": v(-1.15, 8.35) * mm});
            skLineSegment(sketch, "E88.1", {"start": v(-1.6, 15.03) * mm, "end": v(2.6, 15.03) * mm});
            skLineSegment(sketch, "E88.2", {"start": v(-5.46, 8.33) * mm, "end": v(-1.6, 15.03) * mm});
            skLineSegment(sketch, "E88.3", {"start": v(-1.15, 8.35) * mm, "end": v(-5.46, 8.33) * mm});
            skSolve(sketch);
        }
        {
            var Q0;
            Q0=qCreatedBy(makeId("Front.planeOp"),FACE);
            var sketch = newSketch(context, id + "F15", { "sketchPlane" : qUnion([Q0])});
            skLineSegment(sketch, "E89", {"start": v(0, -0.86) * mm, "end": v(0, 49.02) * mm, "construction": true});
            skArc(sketch, "E90", {"start": v(23.62, 25.4) * mm, "mid": v(16.7, 42.1) * mm, "end": v(0, 49.02) * mm});
            skSolve(sketch);
        }
        {
            var Q0;
            Q0=qSketchRegion(id+"F15",true);
            var Q1;
            Q1=sQuery(id+"F15.wireOp",EDGE,"E90");
            var Q2;
            Q2=sQuery(id+"F1.wireOp",EDGE,"E0");
            revolve(context, id + "F16", {"bodyType" : ToolBodyType.SURFACE, "entities" : qUnion([Q0]), "surfaceEntities" : qUnion([Q1]), "axis" : qUnion([Q2]), "revolveType" : RevolveType.FULL});
        }
        {
            var Q0;
            Q0=qSketchRegion(id+"F14",true);
            var Q1;
            Q1=makeQuery(id+"F14.imprint","IMPRINT",FACE,{"disambiguationData":[TD([[makeQuery(id+"F14.imprint","IMPRINT",EDGE,{"derivedFrom":sQuery(id+"F14.wireOp",EDGE,"E79.0")}),1.0]])]});
            var Q2;
            Q2=makeQuery(id+"F14.imprint","IMPRINT",FACE,{"disambiguationData":[TD([[makeQuery(id+"F14.imprint","IMPRINT",EDGE,{"derivedFrom":sQuery(id+"F14.wireOp",EDGE,"E80.0")}),1.0]])]});
            var Q3;
            Q3=makeQuery(id+"F14.imprint","IMPRINT",FACE,{"disambiguationData":[TD([[makeQuery(id+"F14.imprint","IMPRINT",EDGE,{"derivedFrom":sQuery(id+"F14.wireOp",EDGE,"E79.13")}),1.0]])]});
            var Q4;
            Q4=makeQuery(id+"F14.imprint","IMPRINT",FACE,{"disambiguationData":[TD([[makeQuery(id+"F14.imprint","IMPRINT",EDGE,{"derivedFrom":sQuery(id+"F14.wireOp",EDGE,"E84.0")}),-1.0]])]});
            var Q5;
            Q5=makeQuery(id+"F14.imprint","IMPRINT",FACE,{"disambiguationData":[TD([[makeQuery(id+"F14.imprint","IMPRINT",EDGE,{"derivedFrom":sQuery(id+"F14.wireOp",EDGE,"E83.0")}),-1.0]])]});
            var Q6;
            Q6=makeQuery(id+"F14.imprint","IMPRINT",FACE,{"disambiguationData":[TD([[makeQuery(id+"F14.imprint","IMPRINT",EDGE,{"derivedFrom":sQuery(id+"F14.wireOp",EDGE,"E85.0")}),1.0]])]});
            var Q7;
            Q7=makeQuery(id+"F16.opRevolve","SWEPT_FACE",FACE,{"disambiguationData":[OSD([sQuery(id+"F15.wireOp",EDGE,"E90")])]});
            extrude(context, id + "F17", {"entities" : qUnion([Q0, Q1, Q2, Q3, Q4, Q5, Q6]), "operationType" : NewBodyOperationType.REMOVE, "endBound" : BoundingType.UP_TO_SURFACE, "oppositeDirection" : true, "endBoundEntityFace" : qUnion([Q7]), "depth" : 25.4 * mm});
        }
        {
            var Q0;
            Q0=makeQuery(id+"F16.opRevolve","SWEPT_BODY",BODY,{"disambiguationData":[OSD([sQuery(id+"F15.wireOp",EDGE,"E90")])]});
            deleteBodies(context, id + "F18", {"entities" : qUnion([Q0])});
        }
    });
